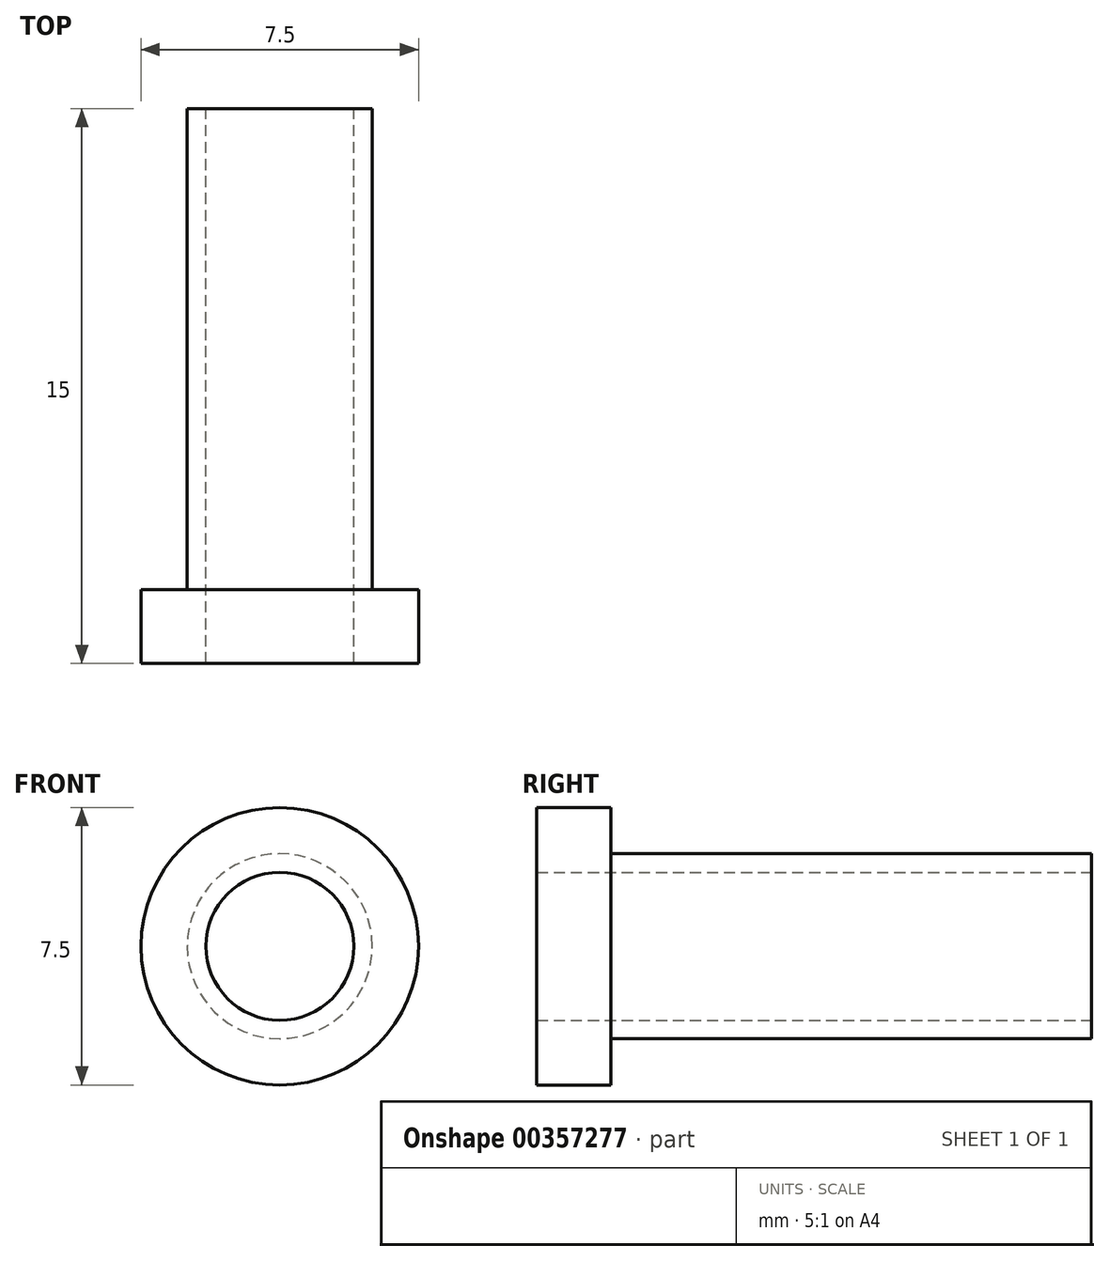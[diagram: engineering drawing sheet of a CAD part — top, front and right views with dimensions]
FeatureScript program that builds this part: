
annotation { "Feature Type Name" : "Feature", "Feature Type Description" : "" }
export const myFeature = defineFeature(function(context is Context, id is Id, definition is map)
    precondition{}
    {
        {
            var Q0;
            Q0=qCreatedBy(makeId("Right.planeOp"),FACE);
            var sketch = newSketch(context, id + "F0", { "sketchPlane" : qUnion([Q0])});
            skLineSegment(sketch, "E0", {"start": v(-9.98, 2) * mm, "end": v(-9.98, 3.75) * mm});
            skLineSegment(sketch, "E1", {"start": v(-9.98, 3.75) * mm, "end": v(-7.98, 3.75) * mm});
            skLineSegment(sketch, "E2", {"start": v(-7.98, 3.75) * mm, "end": v(-7.98, 2.5) * mm});
            skLineSegment(sketch, "E3", {"start": v(-7.98, 2.5) * mm, "end": v(5.02, 2.5) * mm});
            skLineSegment(sketch, "E4", {"start": v(5.02, 2.5) * mm, "end": v(5.02, 2) * mm});
            skLineSegment(sketch, "E5", {"start": v(5.02, 0) * mm, "end": v(-9.98, 0) * mm, "construction": true});
            skLineSegment(sketch, "E6", {"start": v(5.02, 2) * mm, "end": v(-9.98, 2) * mm});
            skSolve(sketch);
        }
        {
            var Q0;
            Q0 = qSketchRegion(id + "F0", true);
            var Q1;
            Q1=sQuery(id+"F0.wireOp",EDGE,"E5");
            revolve(context, id + "F1", {"entities" : qUnion([Q0]), "axis" : qUnion([Q1]), "revolveType" : RevolveType.FULL});
        }
    });
